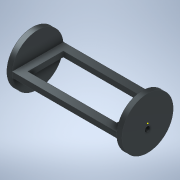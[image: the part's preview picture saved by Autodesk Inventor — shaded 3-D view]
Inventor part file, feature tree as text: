
AUTODESK INVENTOR PART (.ipt)
format: ipt  version: 2020.3 (Build 243373000, 373)  size: 145,920 bytes
history: native  units: mm
features: sketch x4, extrude x3, revolve x1
ambient origin geometry x8: Origin, YZ Plane, XZ Plane, XY Plane, X Axis, Y Axis, Z Axis, Center Point
bodies: Solid1 (feature_tree)
feature tree (8):
  sketch  "Sketch1"  dims[d0=24.5mm d1=5.0mm]
  sketch  "Sketch2"  dims[d2=22.0mm d3=100.0mm]
  revolve  "Revolution1"  [1 undecoded]
  extrude  "Extrusion1"  Depth=100.0mm
  extrude  "Extrusion2"  TaperAngle=90.0deg  [1 undecoded]
  extrude  "Extrusion3"  Depth=49.0mm TaperAngle=0.0deg
  sketch  "Sketch3"  dims[d4=5.0mm d5=90.0deg]
  sketch  "Sketch4"  dims[d6=5.0mm d7=49.0mm d8=0.0mm d9=7.5mm d10=20.0mm d11=0.0mm d13=5.0mm d14=10.0mm d15=0.0mm d16=5.0mm]
note: 2 required parameter values undecoded (feature->parameter linkage not recoverable at this tier; creation-order binding heuristic only, values carry confidence <= 0.55)